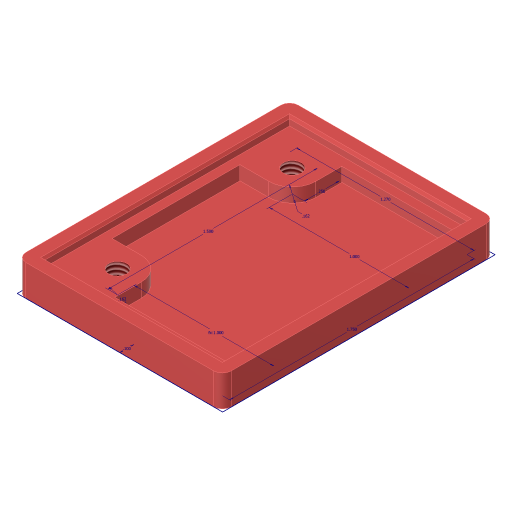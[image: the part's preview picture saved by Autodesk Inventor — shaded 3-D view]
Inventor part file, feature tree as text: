
AUTODESK INVENTOR PART (.ipt)
format: ipt  version: 2023.4 (Build 274418000, 418)  size: 173,568 bytes
history: native  units: in
note: dims shown in document units (in); Inventor stores cm internally (conversion verified against a paired STEP export)
features: sketch x3, extrude x3, hole x1, chamfer x1, fillet x1, projected_geometry x1
ambient origin geometry x8: Origin, YZ Plane, XZ Plane, XY Plane, X Axis, Y Axis, Z Axis, Center Point
bodies: Solid1 (feature_tree)
feature tree (10):
  sketch  "Sketch2"  dims[d0=1.27in d1=1.75in]
  extrude  "Extrusion1"  Depth=1.75in
  extrude  "Extrusion2"  Depth=0.0625in TaperAngle=0.0deg
  sketch  "Sketch5"  dims[d2=0.1in d3=0.0625in d4=0.0in]
  extrude  "Extrusion4"  Depth=0.0625in
  hole  "Hole2"  [1 undecoded]
  chamfer  "Chamfer1"  Distance=0.0625in
  fillet  "Fillet1"  Radius=0.1in
  sketch  "Sketch6"  dims[d5=0.2225in d6=0.0in d23=0.0625in d24=0.0625in d25=0.0625in d26=0.1in d27=0.0in d29=0.375in d31=0.375in d32=1.0in d33=1.0in d34=0.25in d35=1.5in d36=0.13in d37=0.328in d38=0.375in d39=0.25in d40=0.5635in d41=1.0in d42=0.8108in d43=0.162in d44=0.162in d45=0.0157in d46=0.125in d47=45.0deg d48=0.0625in]
  projected_geometry  "Projected Loop2"
note: 1 required parameter value undecoded (feature->parameter linkage not recoverable at this tier; creation-order binding heuristic only, values carry confidence <= 0.55)
